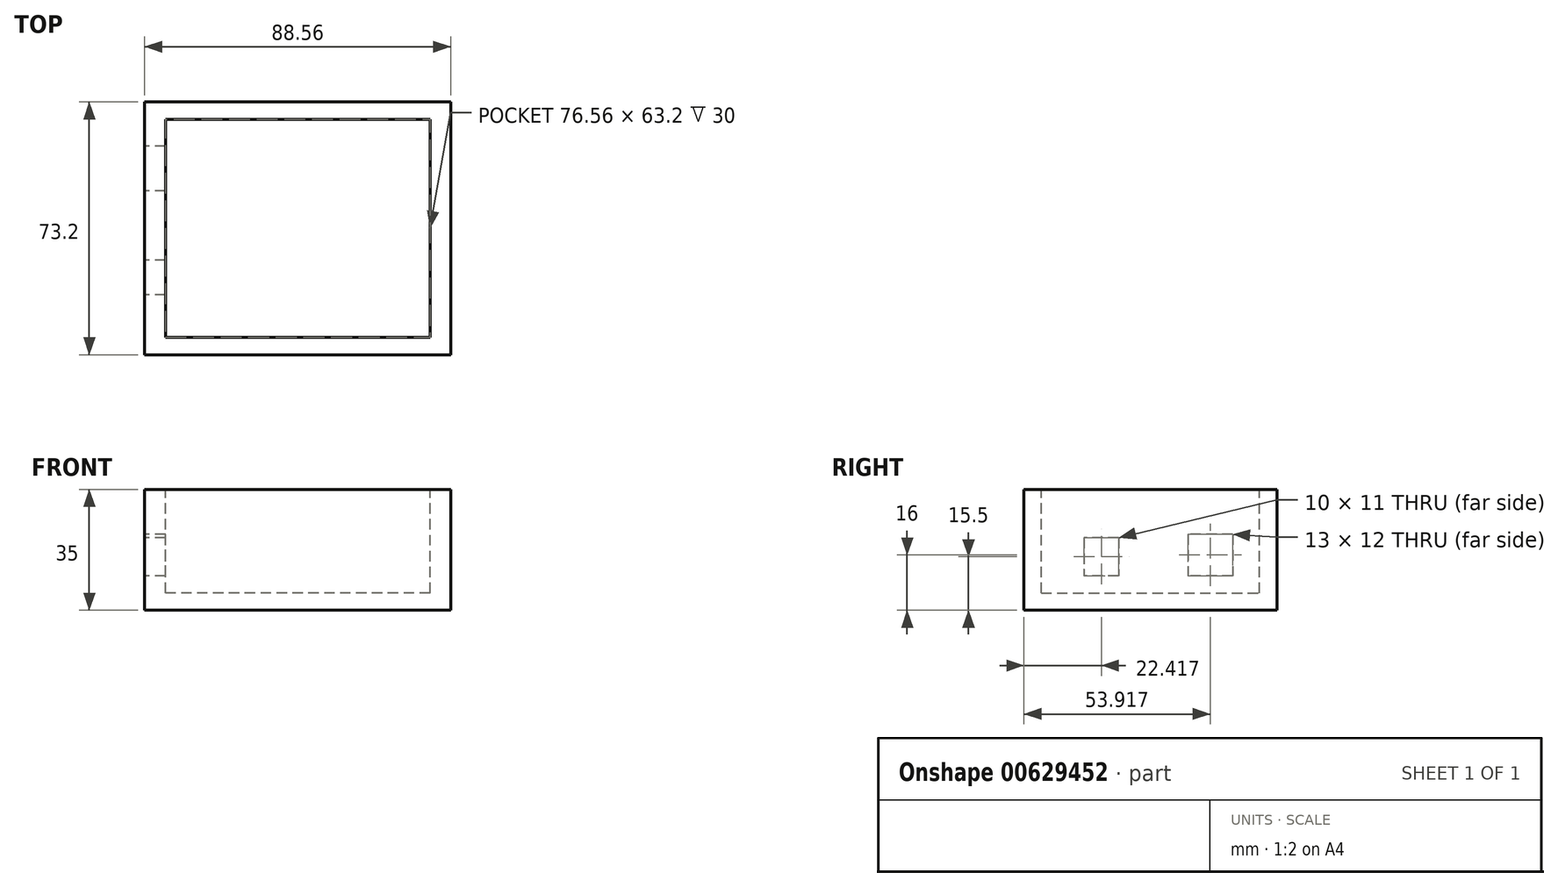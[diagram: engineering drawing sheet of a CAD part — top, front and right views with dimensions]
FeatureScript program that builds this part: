
annotation { "Feature Type Name" : "Feature", "Feature Type Description" : "" }
export const myFeature = defineFeature(function(context is Context, id is Id, definition is map)
    precondition{}
    {
        {
            var Q0;
            Q0=qCreatedBy(makeId("Top.planeOp"),FACE);
            var sketch = newSketch(context, id + "F0", { "sketchPlane" : qUnion([Q0])});
            skLineSegment(sketch, "E0.bottom", {"start": v(-44.28, 36.6) * mm, "end": v(44.28, 36.6) * mm});
            skLineSegment(sketch, "E0.top", {"start": v(-44.28, -36.6) * mm, "end": v(44.28, -36.6) * mm});
            skLineSegment(sketch, "E0.left", {"start": v(-44.28, 36.6) * mm, "end": v(-44.28, -36.6) * mm});
            skLineSegment(sketch, "E0.right", {"start": v(44.28, 36.6) * mm, "end": v(44.28, -36.6) * mm});
            skPoint(sketch, "E0.middle", {"position": v(0, 0) * mm});
            skSolve(sketch);
        }
        {
            var Q0;
            Q0=makeQuery(id+"F0.imprint","IMPRINT",FACE,{"disambiguationData":[TD([[makeQuery(id+"F0.imprint","IMPRINT",EDGE,{"derivedFrom":sQuery(id+"F0.wireOp",EDGE,"E0.bottom")}),-1.0]])]});
            extrude(context, id + "F1", {"entities" : qUnion([Q0]), "oppositeDirection" : true, "depth" : 10 * mm, "offsetDistance" : 25 * mm});
        }
        {
            var Q0;
            Q0=makeQuery(id+"F1.opExtrude","CAP_FACE",FACE,{"disambiguationData":[OSD([sQuery(id+"F0.wireOp",EDGE,"E0.bottom"),sQuery(id+"F0.wireOp",EDGE,"E0.top"),sQuery(id+"F0.wireOp",EDGE,"E0.left"),sQuery(id+"F0.wireOp",EDGE,"E0.right")])],"isStart":true});
            extrude(context, id + "F2", {"entities" : qUnion([Q0]), "operationType" : NewBodyOperationType.ADD, "depth" : 25 * mm, "offsetDistance" : 25 * mm});
        }
        {
            var Q0;
            Q0=makeQuery(id+"F2.opExtrude","CAP_FACE",FACE,{"disambiguationData":[OSD([sQuery(id+"F0.wireOp",EDGE,"E0.bottom"),sQuery(id+"F0.wireOp",EDGE,"E0.top"),sQuery(id+"F0.wireOp",EDGE,"E0.left"),sQuery(id+"F0.wireOp",EDGE,"E0.right")])],"isStart":false});
            var sketch = newSketch(context, id + "F3", { "sketchPlane" : qUnion([Q0])});
            skLineSegment(sketch, "E1.bottom", {"start": v(38.28, -31.6) * mm, "end": v(-38.28, -31.6) * mm});
            skLineSegment(sketch, "E1.top", {"start": v(38.28, 31.6) * mm, "end": v(-38.28, 31.6) * mm});
            skLineSegment(sketch, "E1.left", {"start": v(38.28, -31.6) * mm, "end": v(38.28, 31.6) * mm});
            skLineSegment(sketch, "E1.right", {"start": v(-38.28, -31.6) * mm, "end": v(-38.28, 31.6) * mm});
            skPoint(sketch, "E1.middle", {"position": v(0, 0) * mm});
            skSolve(sketch);
        }
        {
            var Q0;
            Q0=makeQuery(id+"F3.imprint","IMPRINT",FACE,{"disambiguationData":[TD([[makeQuery(id+"F3.imprint","IMPRINT",EDGE,{"derivedFrom":sQuery(id+"F3.wireOp",EDGE,"E1.bottom")}),-1.0]])]});
            extrude(context, id + "F4", {"entities" : qUnion([Q0]), "operationType" : NewBodyOperationType.REMOVE, "oppositeDirection" : true, "depth" : 30 * mm, "offsetDistance" : 25 * mm});
        }
        {
            var Q0;
            {var subQ0=sQuery(id+"F0.wireOp",EDGE,"E0.left");Q0=makeQuery(id+"F2.boolean.opBoolean","MERGE",FACE,{"derivedFrom":[makeQuery(id+"F1.opExtrude","SWEPT_FACE",FACE,{"disambiguationData":[OSD([subQ0])]}),makeQuery(id+"F2.opExtrude","SWEPT_FACE",FACE,{"disambiguationData":[OSD([subQ0])]})]});}
            var sketch = newSketch(context, id + "F5", { "sketchPlane" : qUnion([Q0])});
            skSolve(sketch);
        }
        {
            var Q0;
            {var subQ0=sQuery(id+"F0.wireOp",EDGE,"E0.left");Q0=makeQuery(id+"F5.imprint","IMPRINT",FACE,{"disambiguationData":[TD([[makeQuery(id+"F5.imprint","IMPRINT",EDGE,{"derivedFrom":makeQuery(id+"F1.opExtrude","CAP_EDGE",EDGE,{"disambiguationData":[OSD([subQ0])],"isStart":false})}),1.0]])]});}
            var sketch = newSketch(context, id + "F6", { "sketchPlane" : qUnion([Q0])});
            skLineSegment(sketch, "E2.bottom", {"start": v(-23.82, 12) * mm, "end": v(-10.82, 12) * mm});
            skLineSegment(sketch, "E2.top", {"start": v(-23.82, 0) * mm, "end": v(-10.82, 0) * mm});
            skLineSegment(sketch, "E2.left", {"start": v(-23.82, 12) * mm, "end": v(-23.82, 0) * mm});
            skLineSegment(sketch, "E2.right", {"start": v(-10.82, 12) * mm, "end": v(-10.82, 0) * mm});
            skLineSegment(sketch, "E3.bottom", {"start": v(9.18, 11) * mm, "end": v(19.18, 11) * mm});
            skLineSegment(sketch, "E3.top", {"start": v(9.18, 0) * mm, "end": v(19.18, 0) * mm});
            skLineSegment(sketch, "E3.left", {"start": v(9.18, 11) * mm, "end": v(9.18, 0) * mm});
            skLineSegment(sketch, "E3.right", {"start": v(19.18, 11) * mm, "end": v(19.18, 0) * mm});
            skSolve(sketch);
        }
        {
            var Q0;
            Q0 = qSketchRegion(id + "F6", true);
            extrude(context, id + "F7", {"entities" : qUnion([Q0]), "operationType" : NewBodyOperationType.REMOVE, "oppositeDirection" : true, "depth" : 25 * mm, "offsetDistance" : 25 * mm});
        }
    });
